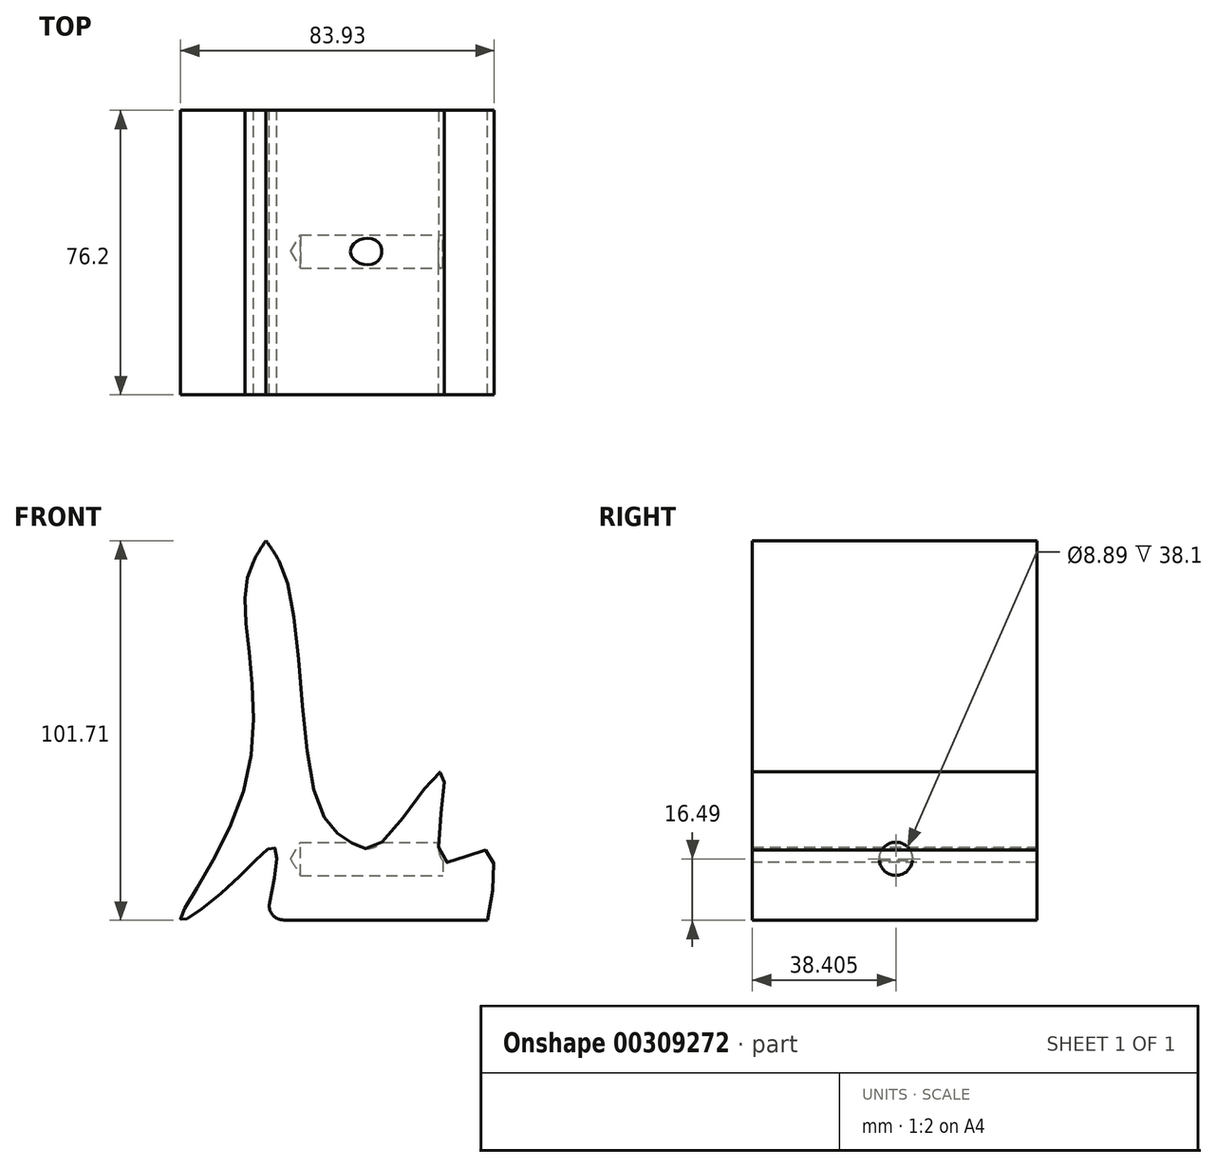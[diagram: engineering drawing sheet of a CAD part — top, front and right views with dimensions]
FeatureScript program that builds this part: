
annotation { "Feature Type Name" : "Feature", "Feature Type Description" : "" }
export const myFeature = defineFeature(function(context is Context, id is Id, definition is map)
    precondition{}
    {
        {
            var Q0;
            Q0=qCreatedBy(makeId("Front.planeOp"),FACE);
            var sketch = newSketch(context, id + "F0", { "sketchPlane" : qUnion([Q0])});
            skLineSegment(sketch, "E0.top", {"start": v(-42.6, -43.66) * mm, "end": v(11.95, -43.66) * mm});
            skFitSpline(sketch, "E1", {"points": [v(-47.34, 57.94) * mm, v(-40.88, 43.78) * mm, v(-33.22, -13) * mm, v(-24.27, -23.08) * mm, v(-16.78, -23.23) * mm, v(0, -4.05) * mm, v(0, -27.75) * mm, v(11.58, -25) * mm, v(11.95, -43.66) * mm], "startDerivative": vector(61.55, -85.52) * mm, "endDerivative": vector(-38.92, -174.93) * mm});
            skFitSpline(sketch, "E2", {"points": [v(-47.34, 57.94) * mm, v(-52.86, 43.95) * mm, v(-52.86, -7.68) * mm, v(-70.07, -43.66) * mm, v(-55.01, -32.58) * mm, v(-45.07, -24.28) * mm, v(-47.34, -43.66) * mm], "startDerivative": vector(-58.21, -88.39) * mm, "endDerivative": vector(-40.72, -184.13) * mm});
            skArc(sketch, "E3.filletArc", {"start": v(-46.34, -39.06) * mm, "mid": v(-45.57, -42.25) * mm, "end": v(-42.6, -43.66) * mm});
            skArc(sketch, "E4.filletArc", {"start": v(-43.83, 52.42) * mm, "mid": v(-47.27, 54.5) * mm, "end": v(-50.66, 52.34) * mm});
            skSolve(sketch);
        }
        {
            var Q0;
            Q0 = qSketchRegion(id + "F0", true);
            extrude(context, id + "F1", {"entities" : qUnion([Q0]), "depth" : 76.2 * mm});
        }
        {
            var Q0;
            Q0=qCreatedBy(makeId("Right.planeOp"),FACE);
            var sketch = newSketch(context, id + "F2", { "sketchPlane" : qUnion([Q0])});
            skPoint(sketch, "E5", {"position": v(-37.8, -27.28) * mm});
            skSolve(sketch);
        }
        {
            var Q0;
            Q0=sQuery(id+"F2.wireOp",VERTEX,"E5");
            var Q1;
            Q1=makeQuery(id+"F1.opExtrude","SWEPT_BODY",BODY,{"disambiguationData":[OSD([sQuery(id+"F0.wireOp",EDGE,"E0.top"),sQuery(id+"F0.wireOp",EDGE,"E1"),sQuery(id+"F0.wireOp",EDGE,"E2"),sQuery(id+"F0.wireOp",EDGE,"E3.filletArc"),sQuery(id+"F0.wireOp",EDGE,"E4.filletArc")])]});
            hole(context, id + "F3", {"style" : HoleStyle.SIMPLE, "endStyle" : HoleEndStyle.BLIND, "holeDiameter" : 8.9 * mm, "holeDepth" : 38.1 * mm, "tappedDepth" : 12.7 * mm, "tapClearance" : 3, "startFromSketch" : true, "locations" : qUnion([Q0]), "scope" : qUnion([Q1])});
        }
    });
